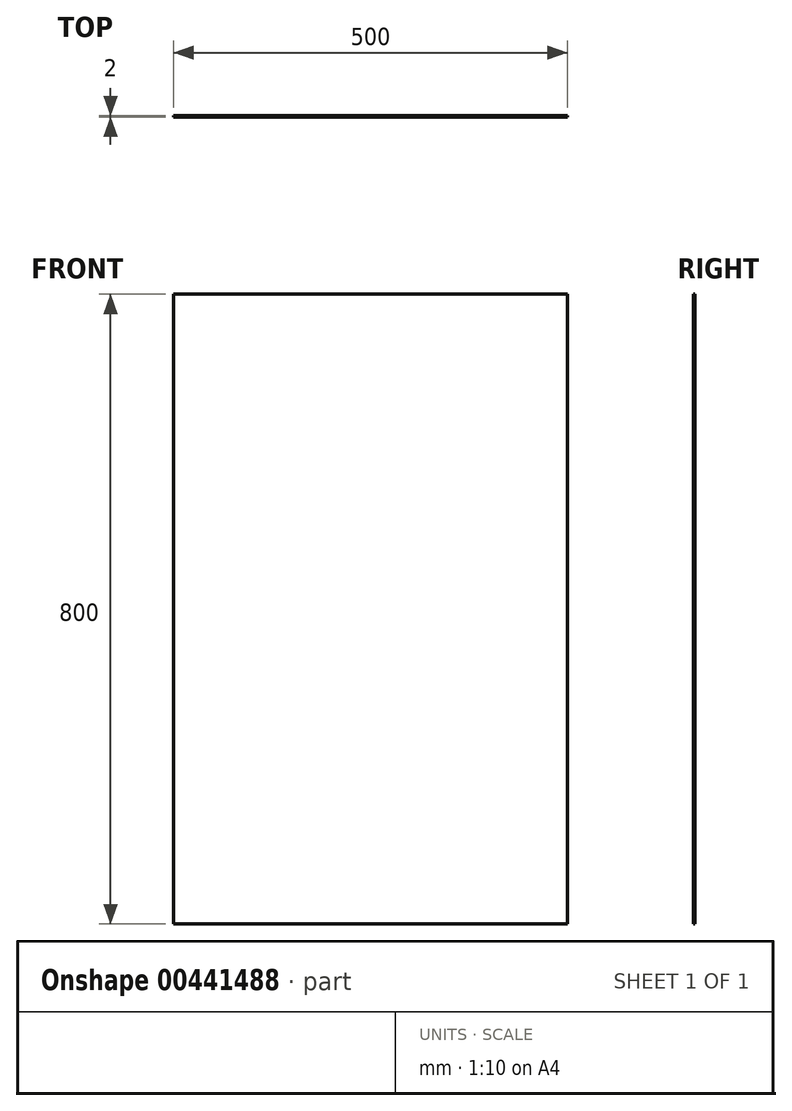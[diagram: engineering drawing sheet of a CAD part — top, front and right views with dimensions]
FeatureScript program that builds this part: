
annotation { "Feature Type Name" : "Feature", "Feature Type Description" : "" }
export const myFeature = defineFeature(function(context is Context, id is Id, definition is map)
    precondition{}
    {
        {
            var Q0;
            Q0=qCreatedBy(makeId("Front.planeOp"),FACE);
            var sketch = newSketch(context, id + "F0", { "sketchPlane" : qUnion([Q0])});
            skLineSegment(sketch, "E0.bottom", {"start": v(250, 400) * mm, "end": v(-250, 400) * mm});
            skLineSegment(sketch, "E0.top", {"start": v(250, -400) * mm, "end": v(-250, -400) * mm});
            skLineSegment(sketch, "E0.left", {"start": v(250, 400) * mm, "end": v(250, -400) * mm});
            skLineSegment(sketch, "E0.right", {"start": v(-250, 400) * mm, "end": v(-250, -400) * mm});
            skPoint(sketch, "E0.middle", {"position": v(0, 0) * mm});
            skSolve(sketch);
        }
        {
            var Q0;
            Q0 = qSketchRegion(id + "F0", true);
            extrude(context, id + "F1", {"entities" : qUnion([Q0]), "endBound" : BoundingType.SYMMETRIC, "depth" : 2 * mm});
        }
    });
